# Revit family: KingswayGroup_DrStps_FloorMountedDoorStop
name_source: partatom
category: Specialty Equipment
units: mm (PartAtom-declared; Revit-internal decimal feet)

## family parameters
Always vertical = Yes
Cut with Voids When Loaded = No
Part Type = Normal
Room Calculation Point = No
Round Connector Dimension = Use Diameter
Shared = No
Work Plane-Based = No

## types (1)
- KingswayGroup_DrStps_FloorMountedDoorStop
    AssetType = Fixed
    BIMObjectName = KingswayGroup_DoorStops_FloorMountedDoorStop
    Category = Pr_30_36_33_24:Door stops
    Color = For full range of available finishes and colours, contact Kingsway Group
    Default Elevation = 0 mm  [stored 0 ft]
    Description = SENTRY Floor Mounted Door Stop
    DurationUnit = year
    Features = Anti-ligature by design and manufactured from cast aluminium with a durable rubber stop, the KG187 provides full support to the door leaf when opened, preventing overextension and impacts with adjacent surfaces.
    Finish = For full range of available finishes and colours, contact Kingsway Group
    IfcExportAs = IfcDiscreteAccessoryType
    IfcExportType = USERDEFINED
    Manufacturer = Kingsway Group
    ManufacturerName = Kingsway Group
    ManufacturerURL = https://kingswaygroupglobal.com
    Material = Cast Aluminium, Rubber
    Model = KG187
    ModelNumber = KG187
    ModelReference = Floor Mounted Door Stop
    Name = DoorStops_FloorMountedDoorStop_KG187_KingswayGroup
    NominalHeight = 0 mm  [stored 0 ft]
    NominalLength = 0 mm  [stored 0 ft]
    NominalWidth = 0 mm  [stored 0 ft]
    PlateMaterial = NBS_Concept
    ProductInformation = https://kingswaygroupglobal.com
    RubberMaterial = NBS_Concept
    URL = https://kingswaygroupglobal.com
    Uniclass2015Code = Pr_30_36_33_24
    Uniclass2015Title = Door stops
    Uniclass2015Version = Products v1.36
    Version = 1
    WarrantyDescription = 5-Year Guarantee *For faulty manufacture and not for damage
    WarrantyDurationParts = 5
    WarrantyDurationUnit = year

note: [stored X ft] marks values corroborated as IEEE doubles in the binary element streams (Revit-internal decimal feet)

## geometry (parser evidence)
native form markers: Sweep x3
no freeform markers — native parametric forms only
